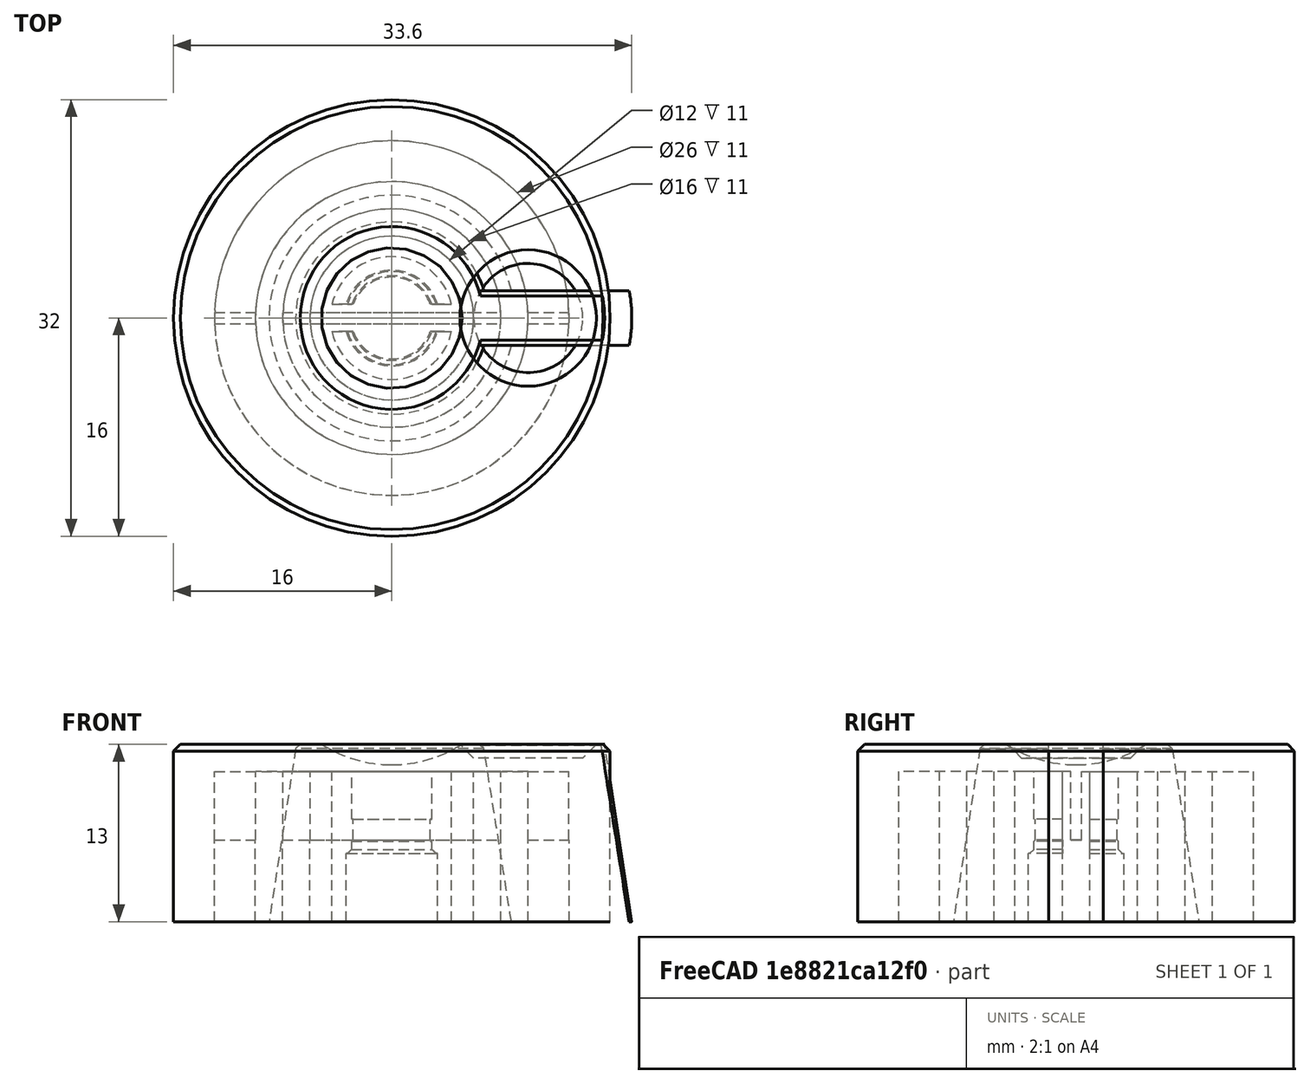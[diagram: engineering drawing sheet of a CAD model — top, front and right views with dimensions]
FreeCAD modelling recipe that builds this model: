
FCSTD DOCUMENT  (FreeCAD 0.18R14555 (Git shallow))
Label: knob
License: All rights reserved
LicenseURL: http://en.wikipedia.org/wiki/All_rights_reserved
objects: Part::Cut×13, Part::Cylinder×12, Part::Box×5, Part::Chamfer×5, Part::Cone×3, Part::MultiFuse×3, Part::Sphere×2, Part::MultiCommon×2, Part::Feature×1
note: 46 computed .brp shape members not serialized (recipe doc carries the construction recipe); baked Part::Feature solids carry a one-line shape summary decoded from their .brp

FEATURE [Part::Cone] Cone
  Angle = 360
  AttacherType = Attacher::AttachEngine3D
  Height = 13
  Radius1 = 9
  Radius2 = 7
FEATURE [Part::Box] Box  label="Cube"
  AttacherType = Attacher::AttachEngine3D
  Height = 13
  Length = 18
  Placement = pos=(0,-2,0) rot=(0,0,1;0rad)
  Width = 4
FEATURE [Part::Cone] Cone001
  Angle = 360
  AttacherType = Attacher::AttachEngine3D
  Height = 13
  Placement = pos=(8,0,0) rot=(0,0,1;0rad)
  Radius1 = 10
  Radius2 = 8
FEATURE [Part::Sphere] Sphere
  Angle1 = -90
  Angle2 = 90
  Angle3 = 360
  AttacherType = Attacher::AttachEngine3D
  Placement = pos=(0,0,32.4) rot=(0,0,1;0rad)
  Radius = 20
FEATURE [Part::Cylinder] Cylinder
  Angle = 360
  AttacherType = Attacher::AttachEngine3D
  Height = 11
  Radius = 4.5
FEATURE [Part::Cylinder] Cylinder001
  Angle = 360
  AttacherType = Attacher::AttachEngine3D
  Height = 11
  Radius = 3.1
FEATURE [Part::Cylinder] Cylinder002
  Angle = 360
  AttacherType = Attacher::AttachEngine3D
  Height = 5
  Radius = 3.5
FEATURE [Part::Cylinder] Cylinder003
  Angle = 360
  AttacherType = Attacher::AttachEngine3D
  Height = 11
  Radius = 6
FEATURE [Part::Box] Box001  label="Cube001"
  AttacherType = Attacher::AttachEngine3D
  Height = 11
  Length = 10
  Placement = pos=(-5,-1,0) rot=(0,0,1;0rad)
  Width = 2
FEATURE [Part::Box] Box002  label="Cube002"
  AttacherType = Attacher::AttachEngine3D
  Height = 5
  Length = 28
  Placement = pos=(-14.5,-0.4,6) rot=(0,0,1;0rad)
  Width = 0.8
FEATURE [Part::MultiCommon] Common
  Shapes = -> [Cone001,Box]
FEATURE [Part::Cylinder] Cylinder004
  Angle = 360
  AttacherType = Attacher::AttachEngine3D
  Height = 17
  Placement = pos=(2.3,0,5e-16) rot=(0,1,0;1.5708rad)
  Radius = 13.1
FEATURE [Part::MultiCommon] Common001
  Shapes = -> [Common,Cylinder004]
FEATURE [Part::Feature] Cone002
  shape: bbox 16 x 16 x 13 mm, 3 faces (baked)
FEATURE [Part::Cut] Cut
  Base = -> Common001
  Tool = -> Cone002
FEATURE [Part::Cone] Cone003
  Angle = 360
  AttacherType = Attacher::AttachEngine3D
  Height = 13
  Radius1 = 9
  Radius2 = 7
FEATURE [Part::Cut] Cut004
  Base = -> Cut
  Placement = pos=(-0.4,0,0) rot=(0,0,1;0rad)
  Tool = -> Cone003
FEATURE [Part::Cut] Cut005
  Base = -> Cone
  Tool = -> Cylinder003
FEATURE [Part::Cut] Cut006
  Base = -> Cut005
  Tool = -> Sphere
FEATURE [Part::Chamfer] Chamfer001
  Base = -> Cut006
  Edges = 2 edges r=0.3: [Edge1,Edge4]
FEATURE [Part::Cut] Cut007
  Base = -> Cylinder
  Tool = -> Cylinder001
FEATURE [Part::Cut] Cut008
  Base = -> Cut007
  Tool = -> Cylinder002
FEATURE [Part::Chamfer] Chamfer
  Base = -> Cut008
  Edges = 1 edges r=0.3: [Edge7]
FEATURE [Part::Cut] Cut009
  Base = -> Chamfer
  Tool = -> Box001
FEATURE [Part::Cylinder] Cylinder005
  Angle = 360
  AttacherType = Attacher::AttachEngine3D
  Height = 13
  Radius = 16
FEATURE [Part::Cylinder] Cylinder006
  Angle = 360
  AttacherType = Attacher::AttachEngine3D
  Height = 11
  Radius = 13
FEATURE [Part::Cut] Cut010
  Base = -> Cylinder005
  Tool = -> Cylinder006
FEATURE [Part::Chamfer] Chamfer002
  Base = -> Cut010
  Edges = 1 edges r=0.5: [Edge1]
FEATURE [Part::Cylinder] Cylinder007
  Angle = 360
  AttacherType = Attacher::AttachEngine3D
  Height = 2
  Placement = pos=(0,0,19) rot=(0,0,1;0rad)
  Radius = 5
FEATURE [Part::Chamfer] Chamfer003
  Base = -> Cylinder007
  Edges = 1 edges r=1: [Edge3]
  Placement = pos=(10,0,-7) rot=(0,0,1;0rad)
FEATURE [Part::Cut] Cut011
  Base = -> Chamfer002
  Tool = -> Chamfer003
FEATURE [Part::Cylinder] Cylinder008
  Angle = 360
  AttacherType = Attacher::AttachEngine3D
  Height = 11
  Radius = 10
FEATURE [Part::Cylinder] Cylinder009
  Angle = 360
  AttacherType = Attacher::AttachEngine3D
  Height = 11
  Radius = 8
FEATURE [Part::Cut] Cut012
  Base = -> Cylinder008
  Tool = -> Cylinder009
FEATURE [Part::Box] Box003  label="Cube003"
  AttacherType = Attacher::AttachEngine3D
  Height = 5
  Length = 14
  Placement = pos=(-6.5,-0.4,6) rot=(0,0,1;0rad)
  Width = 0.8
FEATURE [Part::MultiFuse] Fusion  label="big-knob"
  Shapes = -> [Cut011,Cut012,Box002]
FEATURE [Part::Sphere] Sphere001
  Angle1 = -90
  Angle2 = 90
  Angle3 = 360
  AttacherType = Attacher::AttachEngine3D
  Placement = pos=(0,0,21) rot=(0,0,1;0rad)
  Radius = 9.5
FEATURE [Part::Cut] Cut013
  Base = -> Chamfer001
  Tool = -> Sphere001
FEATURE [Part::MultiFuse] Fusion001  label="prusa-knob"
  Shapes = -> [Cut004,Box003,Cut013]
FEATURE [Part::Cylinder] Cylinder010
  Angle = 360
  AttacherType = Attacher::AttachEngine3D
  Height = 2
  Radius = 3
FEATURE [Part::Cylinder] Cylinder011
  Angle = 360
  AttacherType = Attacher::AttachEngine3D
  Height = 2
  Radius = 4
FEATURE [Part::Cut] Cut014
  Base = -> Cylinder011
  Placement = pos=(0,0,5.5) rot=(0,0,1;0rad)
  Tool = -> Cylinder010
FEATURE [Part::Chamfer] Chamfer005
  Base = -> Cut014
  Edges = 1 edges r=0.5: [Edge5]
FEATURE [Part::Box] Box005  label="Cube005"
  AttacherType = Attacher::AttachEngine3D
  Height = 10
  Length = 10
  Placement = pos=(-5,-1,0) rot=(0,0,1;0rad)
  Width = 2
FEATURE [Part::Cut] Cut015
  Base = -> Chamfer005
  Tool = -> Box005
FEATURE [Part::MultiFuse] Fusion002
  Shapes = -> [Cut009,Cut015]
